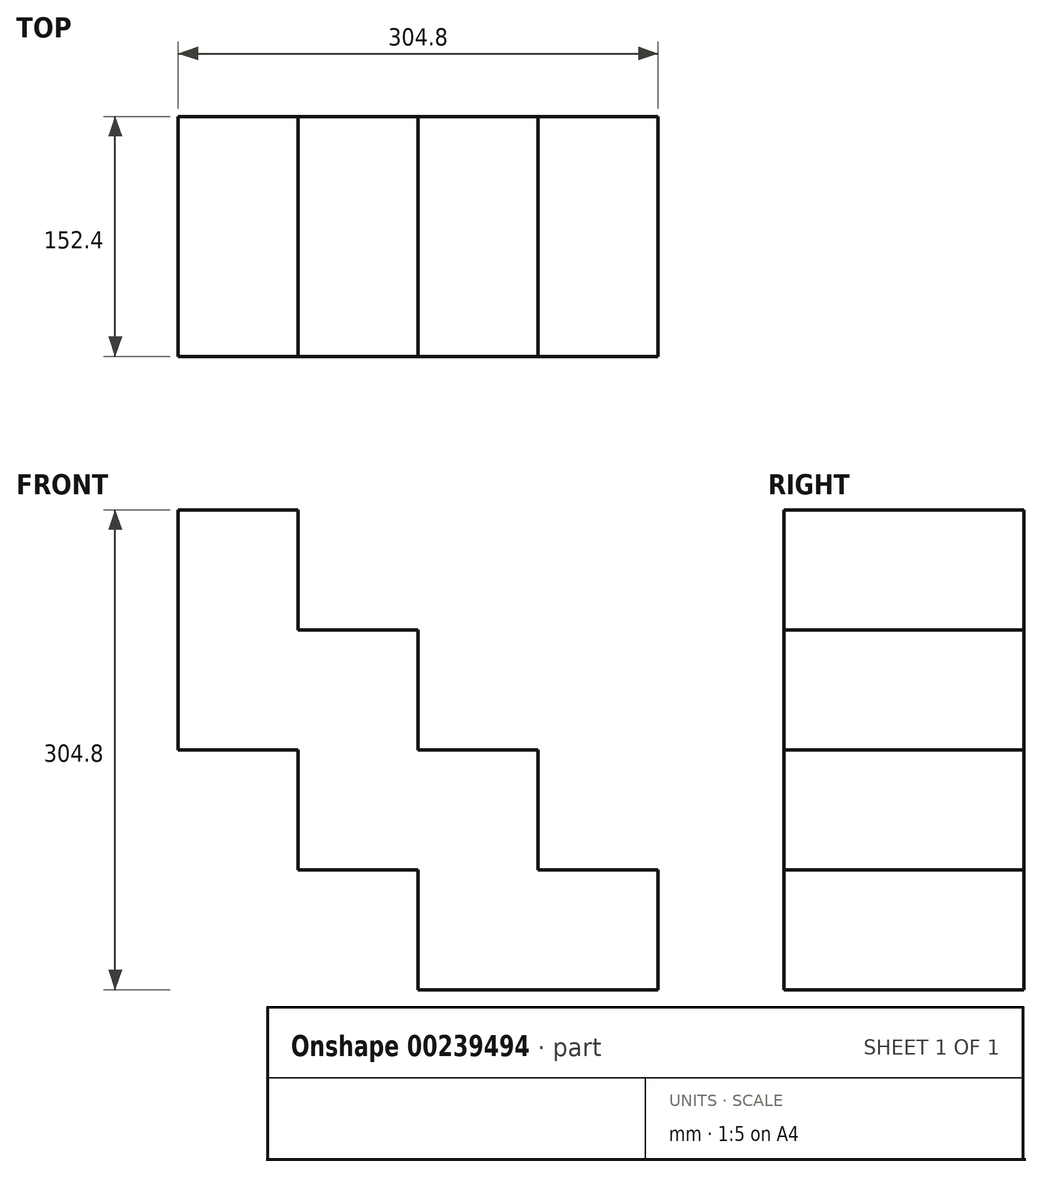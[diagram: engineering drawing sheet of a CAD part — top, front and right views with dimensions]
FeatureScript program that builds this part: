
annotation { "Feature Type Name" : "Feature", "Feature Type Description" : "" }
export const myFeature = defineFeature(function(context is Context, id is Id, definition is map)
    precondition{}
    {
        {
            var Q0;
            Q0=qCreatedBy(makeId("Front.planeOp"),FACE);
            var sketch = newSketch(context, id + "F0", { "sketchPlane" : qUnion([Q0])});
            skLineSegment(sketch, "E0.bottom", {"start": v(76.2, 76.2) * mm, "end": v(-76.2, 76.2) * mm});
            skLineSegment(sketch, "E0.top", {"start": v(76.2, -76.2) * mm, "end": v(-76.2, -76.2) * mm});
            skLineSegment(sketch, "E0.left", {"start": v(76.2, 76.2) * mm, "end": v(76.2, -76.2) * mm});
            skLineSegment(sketch, "E0.right", {"start": v(-76.2, 76.2) * mm, "end": v(-76.2, -76.2) * mm});
            skPoint(sketch, "E0.middle", {"position": v(0, 0) * mm});
            skSolve(sketch);
        }
        {
            var Q0;
            Q0 = qSketchRegion(id + "F0", true);
            extrude(context, id + "F1", {"entities" : qUnion([Q0]), "depth" : 152.4 * mm});
        }
        {
            var Q0;
            Q0=makeQuery(id+"F1.opExtrude","CAP_FACE",FACE,{"disambiguationData":[OSD([sQuery(id+"F0.wireOp",EDGE,"E0.bottom"),sQuery(id+"F0.wireOp",EDGE,"E0.top"),sQuery(id+"F0.wireOp",EDGE,"E0.left"),sQuery(id+"F0.wireOp",EDGE,"E0.right")])],"isStart":false});
            var sketch = newSketch(context, id + "F2", { "sketchPlane" : qUnion([Q0])});
            skLineSegment(sketch, "E1.bottom", {"start": v(0, 0) * mm, "end": v(76.2, 0) * mm});
            skLineSegment(sketch, "E1.top", {"start": v(0, 76.2) * mm, "end": v(76.2, 76.2) * mm});
            skLineSegment(sketch, "E1.left", {"start": v(0, 0) * mm, "end": v(0, 76.2) * mm});
            skLineSegment(sketch, "E1.right", {"start": v(76.2, 0) * mm, "end": v(76.2, 76.2) * mm});
            skSolve(sketch);
        }
        {
            var Q0;
            Q0 = qSketchRegion(id + "F2", true);
            extrude(context, id + "F3", {"entities" : qUnion([Q0]), "operationType" : NewBodyOperationType.REMOVE, "oppositeDirection" : true, "depth" : 271.78 * mm});
        }
        {
            var Q0;
            Q0=makeQuery(id+"F1.opExtrude","SWEPT_FACE",FACE,{"disambiguationData":[OSD([sQuery(id+"F0.wireOp",EDGE,"E0.right")])]});
            var sketch = newSketch(context, id + "F4", { "sketchPlane" : qUnion([Q0])});
            skLineSegment(sketch, "E2.bottom", {"start": v(0, 76.2) * mm, "end": v(152.4, 76.2) * mm});
            skLineSegment(sketch, "E2.top", {"start": v(0, 0) * mm, "end": v(152.4, 0) * mm});
            skLineSegment(sketch, "E2.left", {"start": v(0, 76.2) * mm, "end": v(0, 0) * mm});
            skLineSegment(sketch, "E2.right", {"start": v(152.4, 76.2) * mm, "end": v(152.4, 0) * mm});
            skSolve(sketch);
        }
        {
            var Q0;
            Q0 = qSketchRegion(id + "F4", true);
            extrude(context, id + "F5", {"entities" : qUnion([Q0]), "operationType" : NewBodyOperationType.ADD, "endBound" : BoundingType.SYMMETRIC, "depth" : 152.4 * mm});
        }
        {
            var Q0;
            Q0=makeQuery(id+"F1.opExtrude","SWEPT_FACE",FACE,{"disambiguationData":[OSD([sQuery(id+"F0.wireOp",EDGE,"E0.top")])]});
            var sketch = newSketch(context, id + "F6", { "sketchPlane" : qUnion([Q0])});
            skLineSegment(sketch, "E3.bottom", {"start": v(76.2, 0) * mm, "end": v(0, 0) * mm});
            skLineSegment(sketch, "E3.top", {"start": v(76.2, 152.4) * mm, "end": v(0, 152.4) * mm});
            skLineSegment(sketch, "E3.left", {"start": v(76.2, 0) * mm, "end": v(76.2, 152.4) * mm});
            skLineSegment(sketch, "E3.right", {"start": v(0, 0) * mm, "end": v(0, 152.4) * mm});
            skSolve(sketch);
        }
        {
            var Q0;
            Q0 = qSketchRegion(id + "F6", true);
            extrude(context, id + "F7", {"entities" : qUnion([Q0]), "operationType" : NewBodyOperationType.ADD, "depth" : 76.2 * mm});
        }
        {
            var Q0;
            Q0=makeQuery(id+"F5.boolean.opBoolean","MERGE",FACE,{"derivedFrom":[makeQuery(id+"F1.opExtrude","SWEPT_FACE",FACE,{"disambiguationData":[OSD([sQuery(id+"F0.wireOp",EDGE,"E0.bottom")])]}),makeQuery(id+"F5.opExtrude","SWEPT_FACE",FACE,{"disambiguationData":[OSD([sQuery(id+"F4.wireOp",EDGE,"E2.bottom")])]})]});
            var sketch = newSketch(context, id + "F8", { "sketchPlane" : qUnion([Q0])});
            skLineSegment(sketch, "E4.bottom", {"start": v(-152.4, 0) * mm, "end": v(-76.2, 0) * mm});
            skLineSegment(sketch, "E4.top", {"start": v(-152.4, -152.4) * mm, "end": v(-76.2, -152.4) * mm});
            skLineSegment(sketch, "E4.left", {"start": v(-152.4, 0) * mm, "end": v(-152.4, -152.4) * mm});
            skLineSegment(sketch, "E4.right", {"start": v(-76.2, 0) * mm, "end": v(-76.2, -152.4) * mm});
            skSolve(sketch);
        }
        {
            var Q0;
            Q0 = qSketchRegion(id + "F8", true);
            extrude(context, id + "F9", {"entities" : qUnion([Q0]), "operationType" : NewBodyOperationType.ADD, "depth" : 76.2 * mm});
        }
        {
            var Q0;
            Q0=makeQuery(id+"F7.boolean.opBoolean","MERGE",FACE,{"derivedFrom":[makeQuery(id+"F1.opExtrude","SWEPT_FACE",FACE,{"disambiguationData":[OSD([sQuery(id+"F0.wireOp",EDGE,"E0.left")])]}),makeQuery(id+"F7.opExtrude","SWEPT_FACE",FACE,{"disambiguationData":[OSD([sQuery(id+"F6.wireOp",EDGE,"E3.left")])]})]});
            var sketch = newSketch(context, id + "F10", { "sketchPlane" : qUnion([Q0])});
            skLineSegment(sketch, "E5.bottom", {"start": v(0, -152.4) * mm, "end": v(-152.4, -152.4) * mm});
            skLineSegment(sketch, "E5.top", {"start": v(0, -76.2) * mm, "end": v(-152.4, -76.2) * mm});
            skLineSegment(sketch, "E5.left", {"start": v(0, -152.4) * mm, "end": v(0, -76.2) * mm});
            skLineSegment(sketch, "E5.right", {"start": v(-152.4, -152.4) * mm, "end": v(-152.4, -76.2) * mm});
            skSolve(sketch);
        }
        {
            var Q0;
            Q0 = qSketchRegion(id + "F10", true);
            extrude(context, id + "F11", {"entities" : qUnion([Q0]), "operationType" : NewBodyOperationType.ADD, "endBound" : BoundingType.SYMMETRIC, "depth" : 152.4 * mm});
        }
    });
